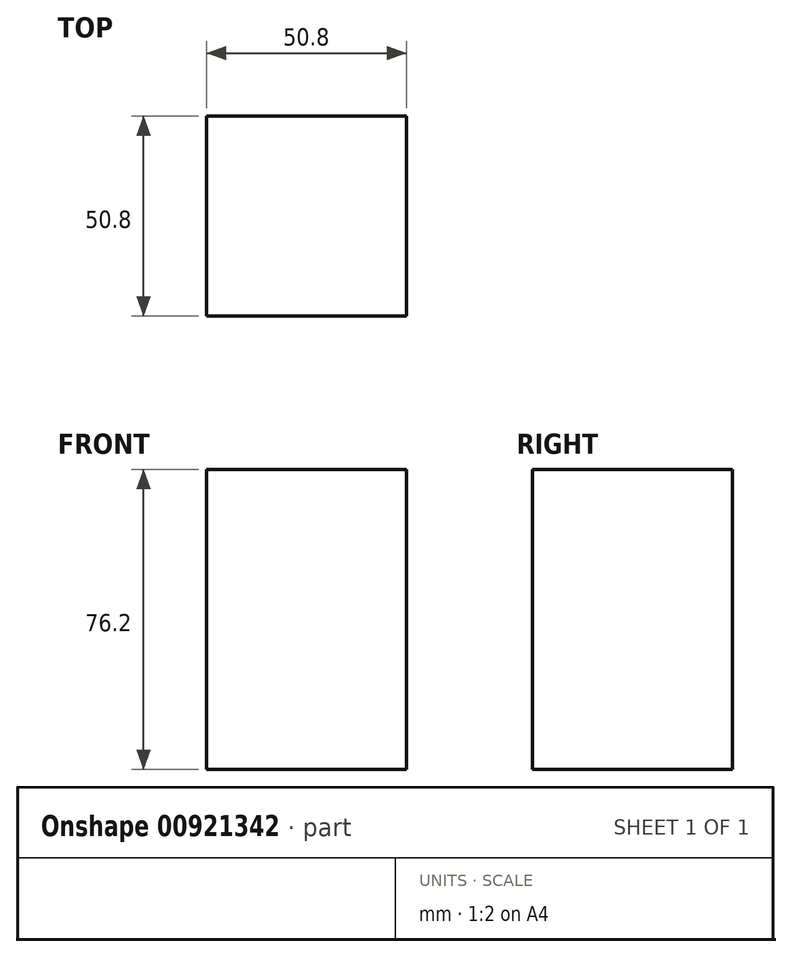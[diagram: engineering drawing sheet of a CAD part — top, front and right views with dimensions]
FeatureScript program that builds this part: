
annotation { "Feature Type Name" : "Feature", "Feature Type Description" : "" }
export const myFeature = defineFeature(function(context is Context, id is Id, definition is map)
    precondition{}
    {
        {
            var Q0;
            Q0=qCreatedBy(makeId("Top.planeOp"),FACE);
            var sketch = newSketch(context, id + "F0", { "sketchPlane" : qUnion([Q0])});
            skLineSegment(sketch, "E0.bottom", {"start": v(-25.4, 25.4) * mm, "end": v(25.4, 25.4) * mm});
            skLineSegment(sketch, "E0.top", {"start": v(-25.4, -25.4) * mm, "end": v(25.4, -25.4) * mm});
            skLineSegment(sketch, "E0.left", {"start": v(-25.4, 25.4) * mm, "end": v(-25.4, -25.4) * mm});
            skLineSegment(sketch, "E0.right", {"start": v(25.4, 25.4) * mm, "end": v(25.4, -25.4) * mm});
            skSolve(sketch);
        }
        {
            var Q0;
            Q0=makeQuery(id+"F0.imprint","IMPRINT",FACE,{"disambiguationData":[TD([[makeQuery(id+"F0.imprint","IMPRINT",EDGE,{"derivedFrom":sQuery(id+"F0.wireOp",EDGE,"E0.bottom")}),-1.0]])]});
            extrude(context, id + "F1", {"entities" : qUnion([Q0]), "depth" : 76.2 * mm, "offsetDistance" : 25.4 * mm});
        }
        {
            var Q0;
            Q0=makeQuery(id+"F1.opExtrude","CAP_FACE",FACE,{"disambiguationData":[OSD([sQuery(id+"F0.wireOp",EDGE,"E0.bottom"),sQuery(id+"F0.wireOp",EDGE,"E0.top"),sQuery(id+"F0.wireOp",EDGE,"E0.left"),sQuery(id+"F0.wireOp",EDGE,"E0.right")])],"isStart":false});
            var sketch = newSketch(context, id + "F2", { "sketchPlane" : qUnion([Q0])});
            skLineSegment(sketch, "E1", {"start": v(25.4, 25.4) * mm, "end": v(-25.4, -25.4) * mm, "construction": true});
            skCircle(sketch, "E2", {"center": v(0, 0) * mm, "radius": 6.35 * mm});
            skSolve(sketch);
        }
        {
            var Q0;
            Q0=sQuery(id+"F2.wireOp",EDGE,"E1");
            var Q1;
            Q1=qCreatedBy(makeId("Front.planeOp"),FACE);
            cPlane(context, id + "F3", {"entities" : qUnion([Q0, Q1]), "cplaneType" : CPlaneType.LINE_ANGLE, "offset" : 25.4 * mm, "angle" : 0 * degree, "width" : 152.4 * mm, "height" : 152.4 * mm});
        }
    });
